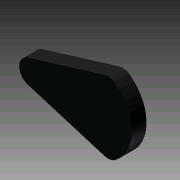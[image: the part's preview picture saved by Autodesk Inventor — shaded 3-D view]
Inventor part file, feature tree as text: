
AUTODESK INVENTOR PART (.ipt)
format: ipt  version: 2011 (Build 150239000, 239)  size: 101,376 bytes
history: native  units: in
note: dims shown in document units (in); Inventor stores cm internally (conversion verified against a paired STEP export)
features: extrude x4, sketch x4
ambient origin geometry x8: Origin, YZ Plane, XZ Plane, XY Plane, X Axis, Y Axis, Z Axis, Center Point
bodies: Solid1 (feature_tree)
feature tree (8):
  extrude  "Extrusion1"  Depth=0.05in TaperAngle=0.0deg
  extrude  "Extrusion2"  Depth=0.05in TaperAngle=0.0deg
  extrude  "Extrusion3"  Depth=0.05in TaperAngle=0.0deg
  extrude  "Extrusion4"  Depth=0.375in
  sketch  "Sketch1"  dims[d0=0.35in d1=0.05in d2=0.0in]
  sketch  "Sketch2"  dims[d3=0.1in d4=0.05in d5=0.0in]
  sketch  "Sketch3"  dims[d6=0.25in d7=0.05in d8=0.0in]
  sketch  "Sketch4"  dims[d9=0.75in d13=0.375in d14=0.25in d15=0.425in d16=0.125in d17=0.15in d18=0.0in d20=0.0in d21=0.875in d22=0.125in]
